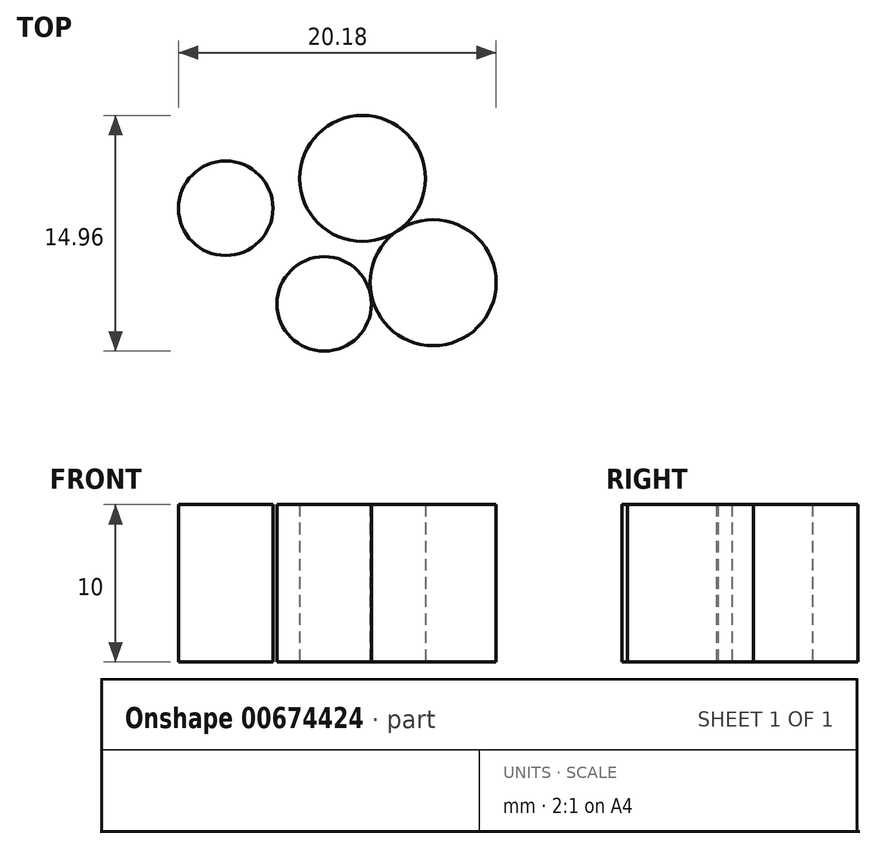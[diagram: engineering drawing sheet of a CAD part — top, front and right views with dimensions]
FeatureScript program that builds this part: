
annotation { "Feature Type Name" : "Feature", "Feature Type Description" : "" }
export const myFeature = defineFeature(function(context is Context, id is Id, definition is map)
    precondition{}
    {
        {
            var Q0;
            Q0=qCreatedBy(makeId("Top.planeOp"),FACE);
            var sketch = newSketch(context, id + "F0", { "sketchPlane" : qUnion([Q0])});
            skCircle(sketch, "E0", {"center": v(0, 0) * mm, "radius": 12 * mm});
            skLineSegment(sketch, "E1", {"start": v(0, 0) * mm, "end": v(0.24, 5) * mm});
            skCircle(sketch, "E2", {"center": v(0.24, 5) * mm, "radius": 4 * mm});
            skLineSegment(sketch, "E3", {"start": v(0, 0) * mm, "end": v(-9.24, 7.65) * mm});
            skLineSegment(sketch, "E4", {"start": v(0, 0) * mm, "end": v(9.93, 6.73) * mm});
            skLineSegment(sketch, "E5", {"start": v(-2.31, 1.91) * mm, "end": v(0.24, 5) * mm});
            skCircle(sketch, "E6", {"center": v(4.73, -1.63) * mm, "radius": 4 * mm});
            skLineSegment(sketch, "E7", {"start": v(0, 0) * mm, "end": v(4.73, -1.63) * mm});
            skLineSegment(sketch, "E8", {"start": v(0, 0) * mm, "end": v(3.68, -11.42) * mm});
            skCircle(sketch, "E9", {"center": v(-8.45, 3.1) * mm, "radius": 3 * mm});
            skLineSegment(sketch, "E10", {"start": v(0, 0) * mm, "end": v(-12, 0.14) * mm});
            skCircle(sketch, "E11", {"center": v(-2.2, -2.97) * mm, "radius": 3 * mm});
            skSolve(sketch);
        }
        {
            var Q0;
            {var subQ0=sQuery(id+"F0.wireOp",EDGE,"E9");var subQ1=makeQuery(id+"F0.imprint","INTERSECT",VERTEX,{"derivedFrom":[sQuery(id+"F0.wireOp",EDGE,"E0"),subQ0]});Q0=makeQuery(id+"F0.imprint","IMPRINT",FACE,{"disambiguationData":[TD([[makeQuery(id+"F0.imprint","IMPRINT",EDGE,{"disambiguationData":[TD([[subQ1,1.0]])],"derivedFrom":subQ0}),1.0]])]});}
            var Q1;
            {var subQ0=sQuery(id+"F0.wireOp",EDGE,"E5");Q1=makeQuery(id+"F0.imprint","IMPRINT",FACE,{"disambiguationData":[TD([[makeQuery(id+"F0.imprint","IMPRINT",EDGE,{"derivedFrom":subQ0}),-1.0]])]});}
            var Q2;
            {var subQ0=sQuery(id+"F0.wireOp",EDGE,"E5");Q2=makeQuery(id+"F0.imprint","IMPRINT",FACE,{"disambiguationData":[TD([[makeQuery(id+"F0.imprint","IMPRINT",EDGE,{"derivedFrom":subQ0}),1.0]])]});}
            var Q3;
            {var subQ0=sQuery(id+"F0.wireOp",EDGE,"E6");var subQ1=makeQuery(id+"F0.imprint","INTERSECT",VERTEX,{"derivedFrom":[subQ0,sQuery(id+"F0.wireOp",EDGE,"E7")]});Q3=makeQuery(id+"F0.imprint","IMPRINT",FACE,{"disambiguationData":[TD([[makeQuery(id+"F0.imprint","IMPRINT",EDGE,{"disambiguationData":[TD([[subQ1,-1.0]])],"derivedFrom":subQ0}),1.0]])]});}
            var Q4;
            {var subQ0=sQuery(id+"F0.wireOp",EDGE,"E11");var subQ1=makeQuery(id+"F0.imprint","INTERSECT",VERTEX,{"derivedFrom":[sQuery(id+"F0.wireOp",EDGE,"E8"),subQ0]});Q4=makeQuery(id+"F0.imprint","IMPRINT",FACE,{"disambiguationData":[TD([[makeQuery(id+"F0.imprint","IMPRINT",EDGE,{"disambiguationData":[TD([[subQ1,-1.0]])],"derivedFrom":subQ0}),1.0]])]});}
            extrude(context, id + "F1", {"entities" : qUnion([Q0, Q1, Q2, Q3, Q4]), "depth" : 10 * mm, "offsetDistance" : 25 * mm});
        }
    });
